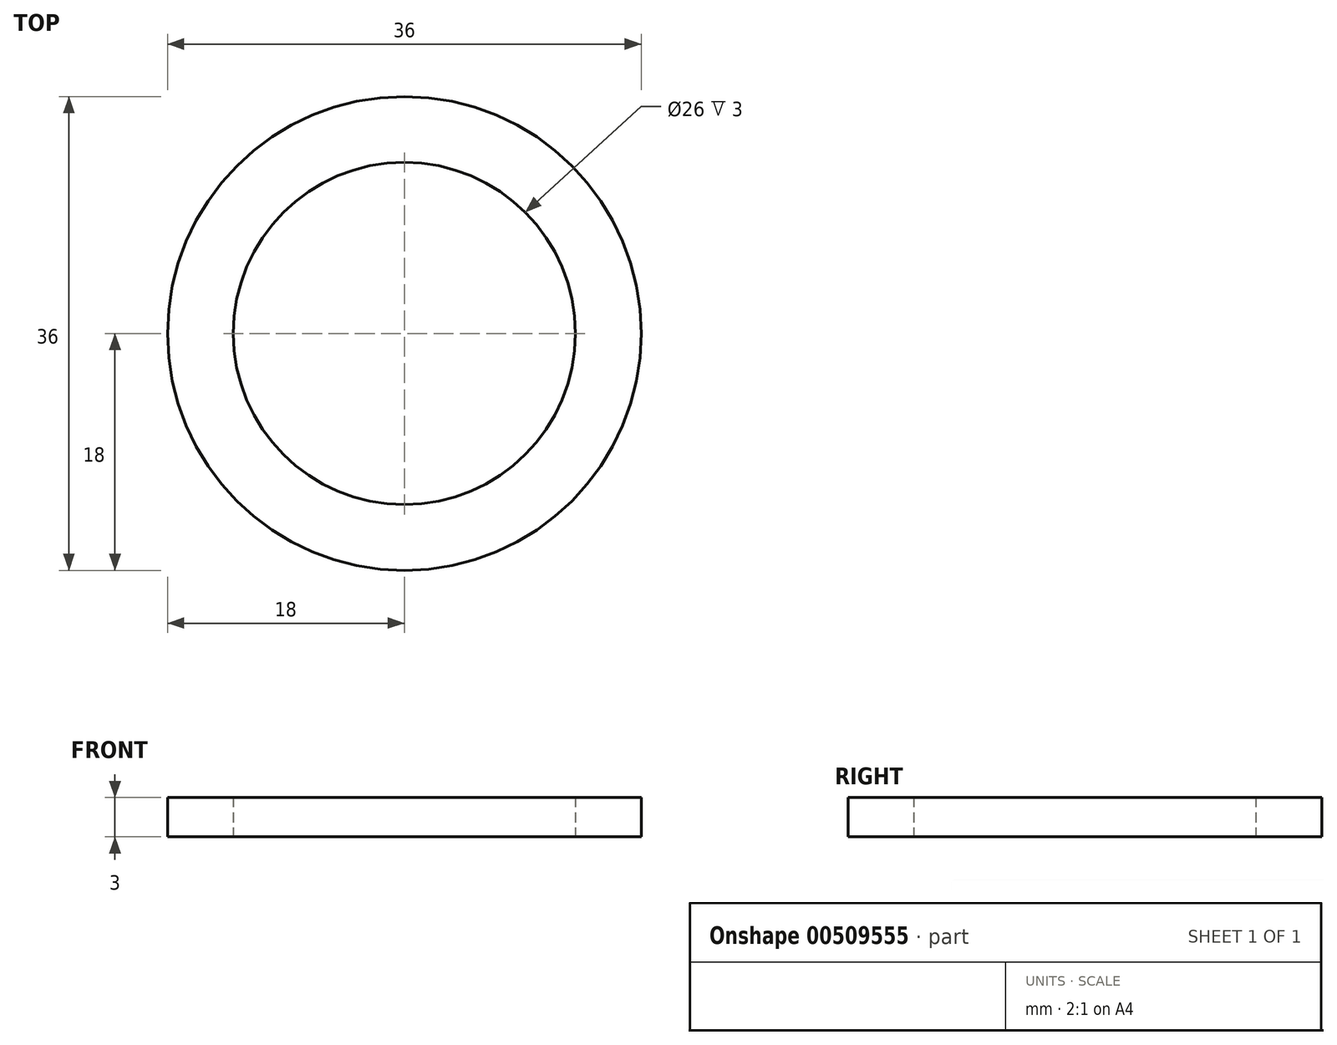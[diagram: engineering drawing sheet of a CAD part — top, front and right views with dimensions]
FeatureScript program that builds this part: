
annotation { "Feature Type Name" : "Feature", "Feature Type Description" : "" }
export const myFeature = defineFeature(function(context is Context, id is Id, definition is map)
    precondition{}
    {
        {
            var Q0;
            Q0=qCreatedBy(makeId("Top.planeOp"),FACE);
            var sketch = newSketch(context, id + "F0", { "sketchPlane" : qUnion([Q0])});
            skCircle(sketch, "E0", {"center": v(0, 0) * mm, "radius": 13 * mm});
            skCircle(sketch, "E1.0", {"center": v(0, 0) * mm, "radius": 18 * mm});
            skSolve(sketch);
        }
        {
            var Q0;
            Q0=makeQuery(id+"F0.imprint","IMPRINT",FACE,{"disambiguationData":[TD([[makeQuery(id+"F0.imprint","IMPRINT",EDGE,{"derivedFrom":sQuery(id+"F0.wireOp",EDGE,"E0")}),-1.0]])]});
            extrude(context, id + "F1", {"entities" : qUnion([Q0]), "depth" : 3 * mm, "offsetDistance" : 25 * mm});
        }
    });
